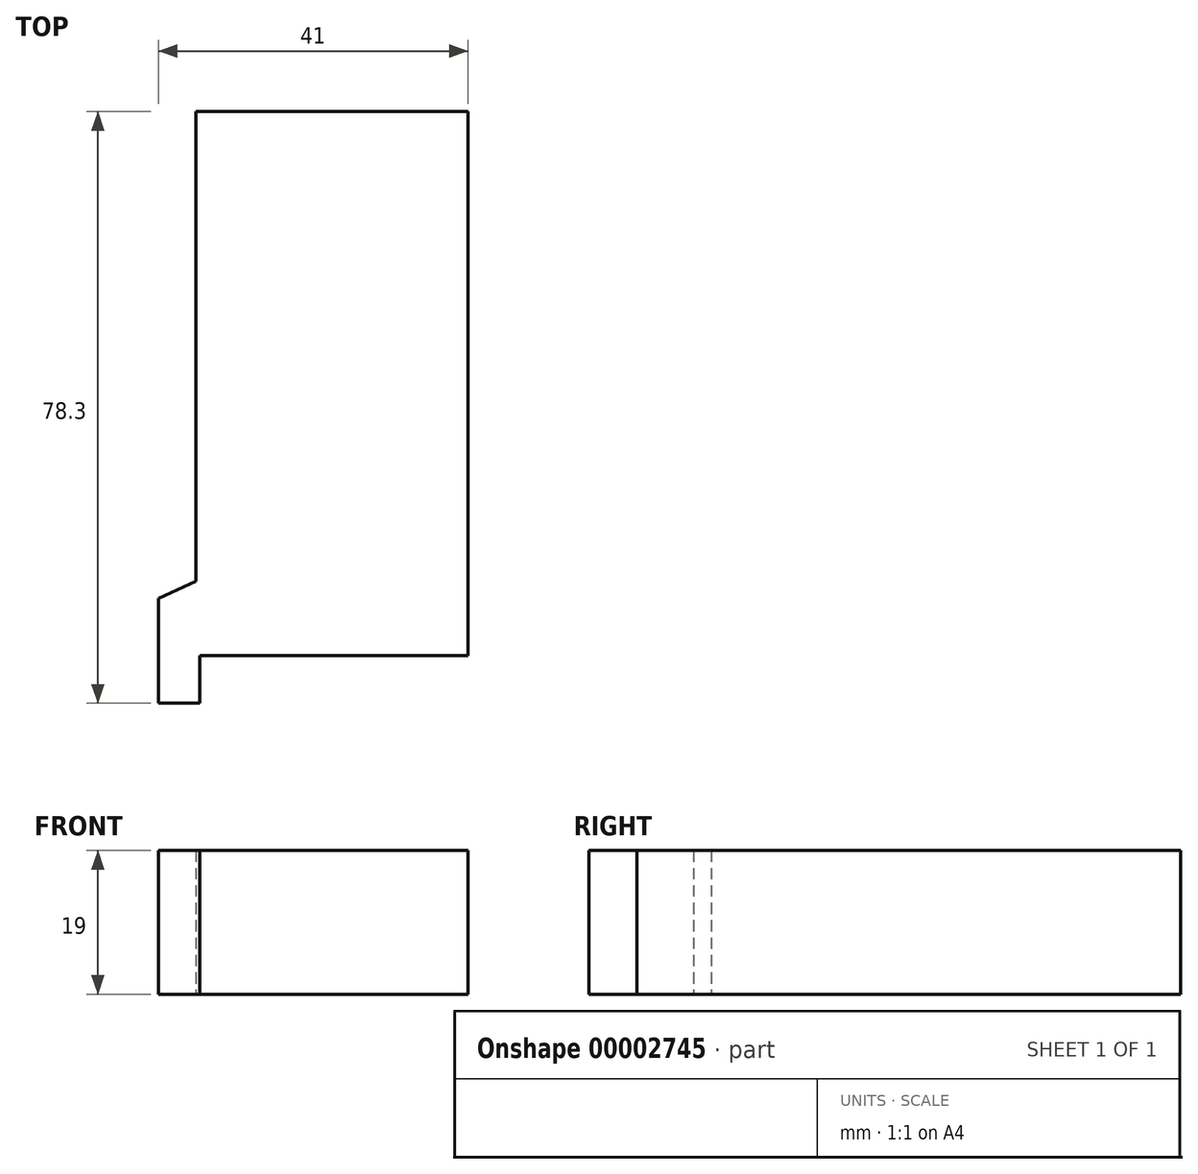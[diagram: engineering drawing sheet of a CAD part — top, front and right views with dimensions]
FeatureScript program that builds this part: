
annotation { "Feature Type Name" : "Feature", "Feature Type Description" : "" }
export const myFeature = defineFeature(function(context is Context, id is Id, definition is map)
    precondition{}
    {
        {
            var Q0;
            Q0=qCreatedBy(makeId("Top.planeOp"),FACE);
            var sketch = newSketch(context, id + "F0", { "sketchPlane" : qUnion([Q0])});
            skLineSegment(sketch, "E0.bottom", {"start": v(-18, 36) * mm, "end": v(18, 36) * mm});
            skLineSegment(sketch, "E0.top", {"start": v(-18, -36) * mm, "end": v(18, -36) * mm});
            skLineSegment(sketch, "E0.left", {"start": v(-18, 36) * mm, "end": v(-18, -36) * mm});
            skLineSegment(sketch, "E0.right", {"start": v(18, 36) * mm, "end": v(18, -36) * mm});
            skPoint(sketch, "E0.middle", {"position": v(0, 0) * mm});
            skLineSegment(sketch, "E1", {"start": v(-18, -26.12) * mm, "end": v(-23, -28.46) * mm});
            skLineSegment(sketch, "E2", {"start": v(-23, -28.46) * mm, "end": v(-23, -42.3) * mm});
            skLineSegment(sketch, "E3", {"start": v(-23, -42.3) * mm, "end": v(-17.54, -42.3) * mm});
            skLineSegment(sketch, "E4", {"start": v(-17.54, -42.3) * mm, "end": v(-17.54, -36) * mm});
            skSolve(sketch);
        }
        {
            var Q0;
            Q0 = qSketchRegion(id + "F0", true);
            extrude(context, id + "F1", {"entities" : qUnion([Q0]), "depth" : 19 * mm});
        }
    });
